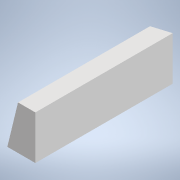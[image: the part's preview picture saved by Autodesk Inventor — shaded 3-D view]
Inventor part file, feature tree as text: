
AUTODESK INVENTOR PART (.ipt)
format: ipt  version: 2020 (Build 240168000, 168)  size: 91,648 bytes
history: native  units: in
note: dims shown in document units (in); Inventor stores cm internally (conversion verified against a paired STEP export)
features: other x8, reference x3, sketch x1, plane x1, extrude x1
ambient origin geometry x8: Origin, YZ Plane, XZ Plane, XY Plane, X Axis, Y Axis, Z Axis, Center Point
bodies: Solid1 (feature_tree)
feature tree (14):
  sketch  "Sketch1"  dims[d0=1.0in d1=0.0in]
  plane  "Work Plane1"
  extrude  "Extrusion1"  [1 undecoded]
  reference  "Reference1"
  reference  "Reference2"
  reference  "Reference3"
  other  "<userpath>\Documents\FRC\2020\Prototype1.iam"
  other  "Prototype1.iam"
  other  "DriveBase2020:1"
  other  "AM14U3 Long Half:2"
  other  "AM14U3 Long Frame Half_3"
  other  "AM14U3 Outside Sheet Rev1_DefaultSM-FLAT-PATTERN_137"
  other  "AM14U3 End Sheet PowerCell_MIR:1"
  other  "AM14U3 End Sheet PowerCell:1"
note: 1 required parameter value undecoded (feature->parameter linkage not recoverable at this tier; creation-order binding heuristic only, values carry confidence <= 0.55)
